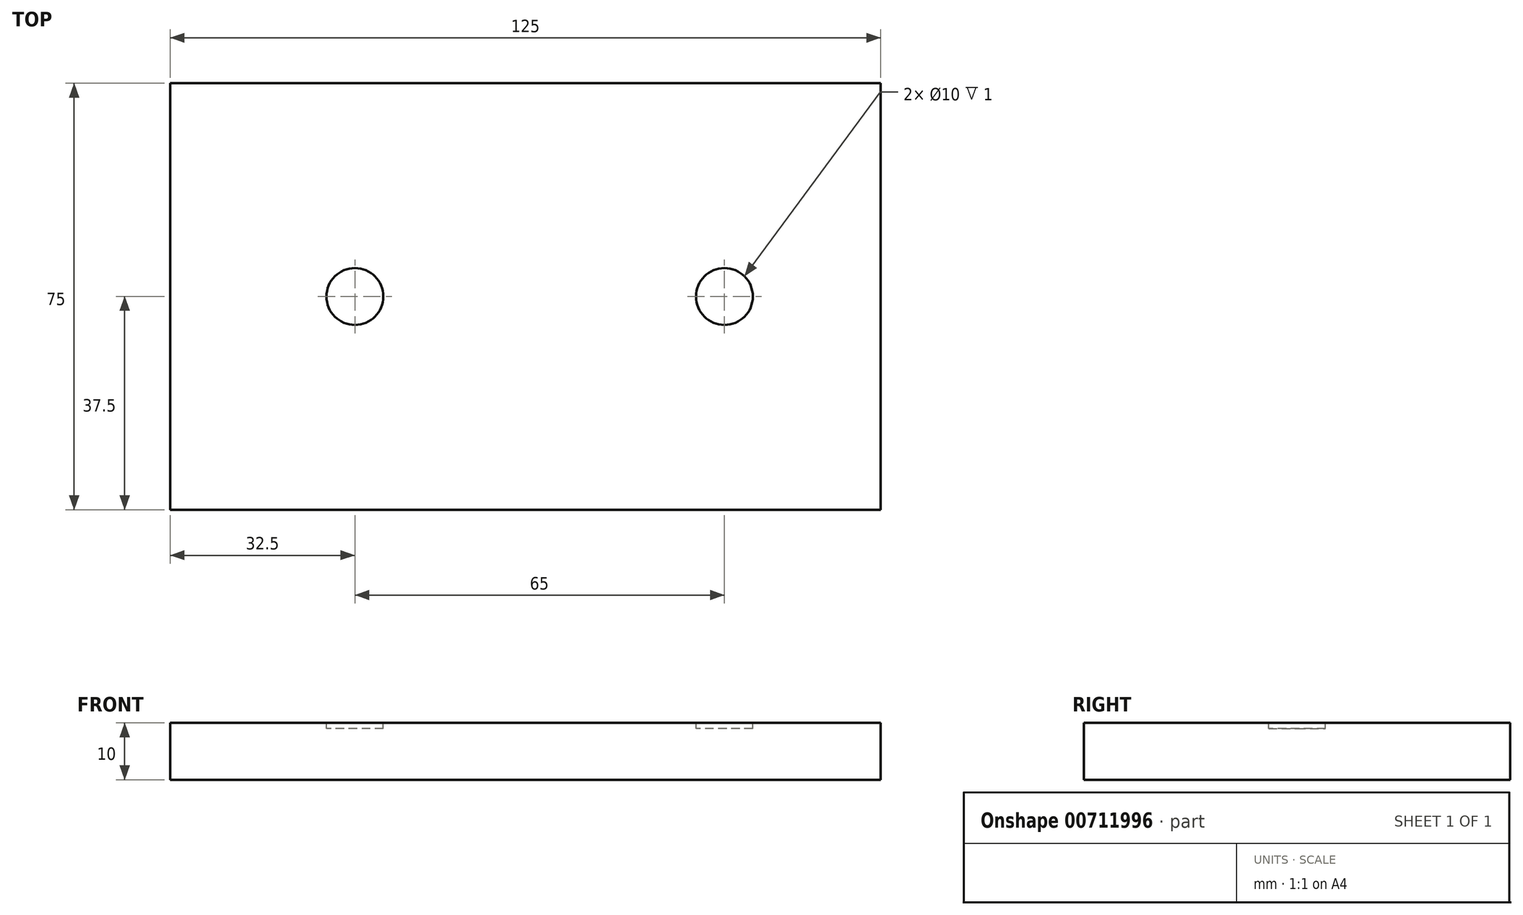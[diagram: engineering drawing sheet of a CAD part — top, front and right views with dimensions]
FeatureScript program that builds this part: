
annotation { "Feature Type Name" : "Feature", "Feature Type Description" : "" }
export const myFeature = defineFeature(function(context is Context, id is Id, definition is map)
    precondition{}
    {
        {
            var Q0;
            Q0=qCreatedBy(makeId("Top.planeOp"),FACE);
            var sketch = newSketch(context, id + "F0", { "sketchPlane" : qUnion([Q0])});
            skLineSegment(sketch, "E0.bottom", {"start": v(0, 0) * mm, "end": v(125, 0) * mm});
            skLineSegment(sketch, "E0.top", {"start": v(0, -75) * mm, "end": v(125, -75) * mm});
            skLineSegment(sketch, "E0.left", {"start": v(0, 0) * mm, "end": v(0, -75) * mm});
            skLineSegment(sketch, "E0.right", {"start": v(125, 0) * mm, "end": v(125, -75) * mm});
            skSolve(sketch);
        }
        {
            var Q0;
            Q0=qSketchRegion(id+"F0",true);
            extrude(context, id + "F1", {"entities" : qUnion([Q0]), "depth" : 10 * mm, "offsetDistance" : 25 * mm});
        }
        {
            var Q0;
            Q0=makeQuery(id+"F1.opExtrude","CAP_FACE",FACE,{"disambiguationData":[OSD([sQuery(id+"F0.wireOp",EDGE,"E0.bottom"),sQuery(id+"F0.wireOp",EDGE,"E0.top"),sQuery(id+"F0.wireOp",EDGE,"E0.left"),sQuery(id+"F0.wireOp",EDGE,"E0.right")])],"isStart":false});
            var sketch = newSketch(context, id + "F2", { "sketchPlane" : qUnion([Q0])});
            skCircle(sketch, "E1", {"center": v(32.5, -37.5) * mm, "radius": 5 * mm});
            skCircle(sketch, "E2", {"center": v(97.5, -37.5) * mm, "radius": 5 * mm});
            skSolve(sketch);
        }
        {
            var Q0;
            Q0=qSketchRegion(id+"F2",true);
            extrude(context, id + "F3", {"entities" : qUnion([Q0]), "operationType" : NewBodyOperationType.REMOVE, "oppositeDirection" : true, "depth" : 1 * mm, "offsetDistance" : 25 * mm});
        }
    });
